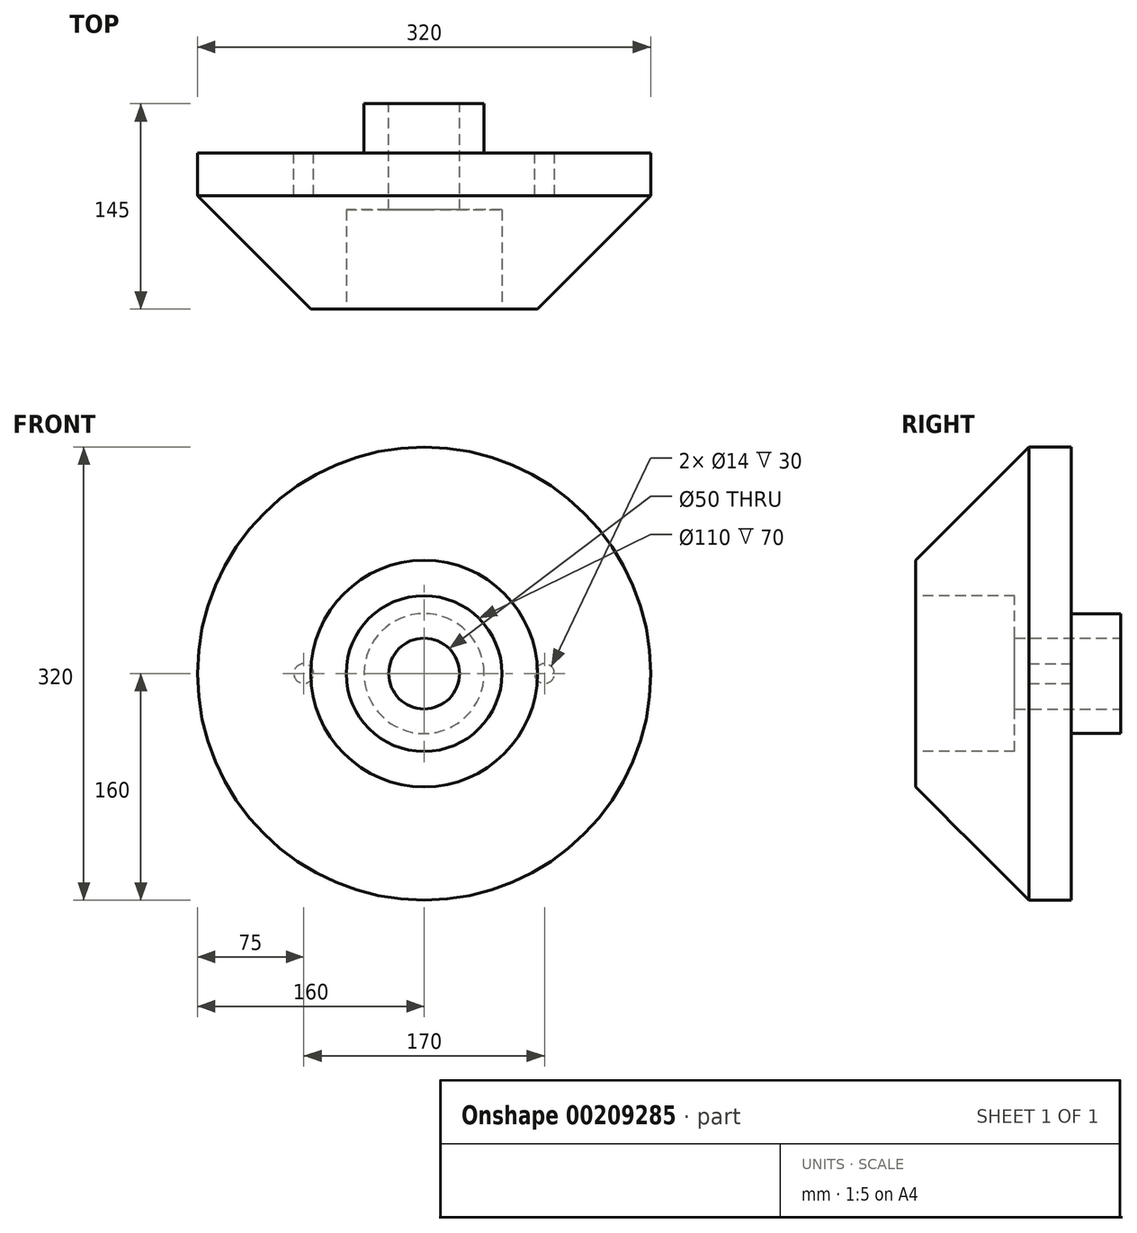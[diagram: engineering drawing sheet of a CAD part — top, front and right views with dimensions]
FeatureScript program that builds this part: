
annotation { "Feature Type Name" : "Feature", "Feature Type Description" : "" }
export const myFeature = defineFeature(function(context is Context, id is Id, definition is map)
    precondition{}
    {
        {
            var Q0;
            Q0=qCreatedBy(makeId("Front.planeOp"),FACE);
            var sketch = newSketch(context, id + "F0", { "sketchPlane" : qUnion([Q0])});
            skCircle(sketch, "E0", {"center": v(0, 0) * mm, "radius": 25 * mm});
            skCircle(sketch, "E1", {"center": v(0, 0) * mm, "radius": 42.35 * mm});
            skCircle(sketch, "E2", {"center": v(0, 0) * mm, "radius": 160 * mm});
            skCircle(sketch, "E3", {"center": v(0, 0) * mm, "radius": 50 * mm});
            skSolve(sketch);
        }
        {
            var Q0;
            Q0=makeQuery(id+"F0.imprint","IMPRINT",FACE,{"disambiguationData":[TD([[makeQuery(id+"F0.imprint","IMPRINT",EDGE,{"derivedFrom":sQuery(id+"F0.wireOp",EDGE,"E2")}),1.0]])]});
            var Q1;
            Q1=makeQuery(id+"F0.imprint","IMPRINT",FACE,{"disambiguationData":[TD([[makeQuery(id+"F0.imprint","IMPRINT",EDGE,{"derivedFrom":sQuery(id+"F0.wireOp",EDGE,"E1")}),-1.0]])]});
            var Q2;
            Q2=makeQuery(id+"F0.imprint","IMPRINT",FACE,{"disambiguationData":[TD([[makeQuery(id+"F0.imprint","IMPRINT",EDGE,{"derivedFrom":sQuery(id+"F0.wireOp",EDGE,"E0")}),-1.0]])]});
            extrude(context, id + "F1", {"entities" : qUnion([Q0, Q1, Q2]), "depth" : 110 * mm});
        }
        {
            var Q0;
            Q0=makeQuery(id+"F0.imprint","IMPRINT",FACE,{"disambiguationData":[TD([[makeQuery(id+"F0.imprint","IMPRINT",EDGE,{"derivedFrom":sQuery(id+"F0.wireOp",EDGE,"E0")}),-1.0]])]});
            extrude(context, id + "F2", {"entities" : qUnion([Q0]), "operationType" : NewBodyOperationType.ADD, "oppositeDirection" : true, "depth" : 35 * mm});
        }
        {
            var Q0;
            Q0=makeQuery(id+"F1.opExtrude","CAP_EDGE",EDGE,{"disambiguationData":[OSD([sQuery(id+"F0.wireOp",EDGE,"E2")])],"isStart":false});
            chamfer(context, id + "F3", {"entities" : qUnion([Q0]), "width" : 80 * mm, "tangentPropagation" : true});
        }
        {
            var Q0;
            Q0=makeQuery(id+"F1.opExtrude","CAP_FACE",FACE,{"disambiguationData":[OSD([sQuery(id+"F0.wireOp",EDGE,"E0"),sQuery(id+"F0.wireOp",EDGE,"E2")])],"isStart":false});
            var sketch = newSketch(context, id + "F4", { "sketchPlane" : qUnion([Q0])});
            skCircle(sketch, "E4", {"center": v(0, 0) * mm, "radius": 55 * mm});
            skSolve(sketch);
        }
        {
            var Q0;
            Q0=makeQuery(id+"F4.imprint","IMPRINT",FACE,{"disambiguationData":[TD([[makeQuery(id+"F4.imprint","IMPRINT",EDGE,{"derivedFrom":sQuery(id+"F4.wireOp",EDGE,"E4")}),1.0]])]});
            extrude(context, id + "F5", {"entities" : qUnion([Q0]), "operationType" : NewBodyOperationType.REMOVE, "oppositeDirection" : true, "depth" : 70 * mm});
        }
        {
            var Q0;
            Q0=makeQuery(id+"F1.opExtrude","CAP_FACE",FACE,{"disambiguationData":[OSD([sQuery(id+"F0.wireOp",EDGE,"E0"),sQuery(id+"F0.wireOp",EDGE,"E2")])],"isStart":true});
            var sketch = newSketch(context, id + "F6", { "sketchPlane" : qUnion([Q0])});
            skLineSegment(sketch, "E5", {"start": v(-179.65, 0) * mm, "end": v(190.17, 0) * mm, "construction": true});
            skCircle(sketch, "E6", {"center": v(-85, 0) * mm, "radius": 7 * mm});
            skCircle(sketch, "E7", {"center": v(85, 0) * mm, "radius": 7 * mm});
            skSolve(sketch);
        }
        {
            var Q0;
            Q0=makeQuery(id+"F6.imprint","IMPRINT",FACE,{"disambiguationData":[TD([[makeQuery(id+"F6.imprint","IMPRINT",EDGE,{"derivedFrom":sQuery(id+"F6.wireOp",EDGE,"E6")}),1.0]])]});
            var Q1;
            Q1=makeQuery(id+"F6.imprint","IMPRINT",FACE,{"disambiguationData":[TD([[makeQuery(id+"F6.imprint","IMPRINT",EDGE,{"derivedFrom":sQuery(id+"F6.wireOp",EDGE,"E7")}),1.0]])]});
            extrude(context, id + "F7", {"entities" : qUnion([Q0, Q1]), "operationType" : NewBodyOperationType.REMOVE, "oppositeDirection" : true, "depth" : 30 * mm});
        }
    });
